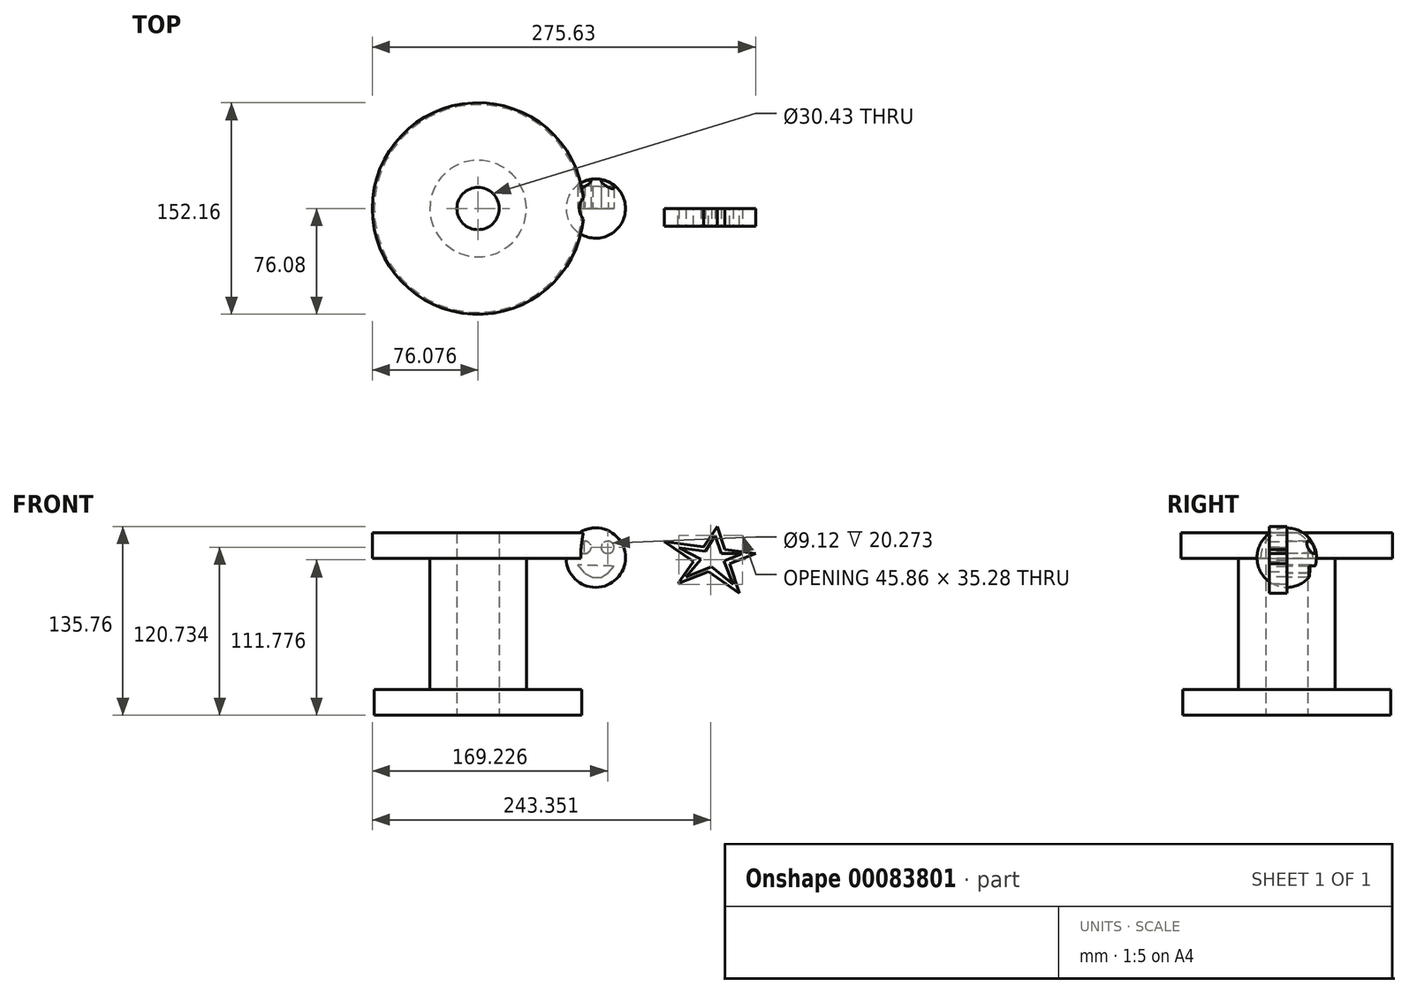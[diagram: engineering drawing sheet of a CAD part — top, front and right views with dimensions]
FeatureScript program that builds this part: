
annotation { "Feature Type Name" : "Feature", "Feature Type Description" : "" }
export const myFeature = defineFeature(function(context is Context, id is Id, definition is map)
    precondition{}
    {
        {
            var Q0;
            Q0=qCreatedBy(makeId("Front.planeOp"),FACE);
            var sketch = newSketch(context, id + "F0", { "sketchPlane" : qUnion([Q0])});
            skLineSegment(sketch, "E0", {"start": v(-32.02, -27.07) * mm, "end": v(-19.27, -67.24) * mm});
            skLineSegment(sketch, "E1", {"start": v(-19.27, -67.24) * mm, "end": v(-2.16, -25.66) * mm});
            skCircle(sketch, "E2", {"center": v(-17.49, -17.95) * mm, "radius": 17.16 * mm});
            skLineSegment(sketch, "E3", {"start": v(18.35, 23.13) * mm, "end": v(46.46, 64.2) * mm});
            skLineSegment(sketch, "E4", {"start": v(46.46, 64.2) * mm, "end": v(62.45, 16.23) * mm});
            skLineSegment(sketch, "E5", {"start": v(62.45, 16.23) * mm, "end": v(8.43, 53.21) * mm});
            skLineSegment(sketch, "E6", {"start": v(8.43, 53.21) * mm, "end": v(74.03, 44.9) * mm});
            skLineSegment(sketch, "E7", {"start": v(74.03, 44.9) * mm, "end": v(18.35, 23.13) * mm});
            skSolve(sketch);
        }
        {
            var Q0;
            Q0 = qSketchRegion(id + "F0", true);
            extrude(context, id + "F1", {"entities" : qUnion([Q0]), "depth" : 12.7 * mm});
        }
        {
            var Q0;
            Q0=makeQuery(id+"F1.opExtrude","CAP_FACE",FACE,{"disambiguationData":[OSD([sQuery(id+"F0.wireOp",EDGE,"E3"),sQuery(id+"F0.wireOp",EDGE,"E4"),sQuery(id+"F0.wireOp",EDGE,"E5"),sQuery(id+"F0.wireOp",EDGE,"E6"),sQuery(id+"F0.wireOp",EDGE,"E7")])],"isStart":false});
            var sketch = newSketch(context, id + "F2", { "sketchPlane" : qUnion([Q0])});
            skLineSegment(sketch, "E8", {"start": v(37.8, 46.38) * mm, "end": v(44.96, 57.86) * mm});
            skLineSegment(sketch, "E9", {"start": v(44.96, 57.86) * mm, "end": v(49.21, 44.66) * mm});
            skPoint(sketch, "E9.endSnap0", {"position": v(49.21, 55.95) * mm});
            skLineSegment(sketch, "E10", {"start": v(49.21, 44.66) * mm, "end": v(64.68, 44.66) * mm});
            skPoint(sketch, "E10.endSnap0", {"position": v(64.68, 41.25) * mm});
            skLineSegment(sketch, "E11", {"start": v(64.68, 44.66) * mm, "end": v(51.28, 39.42) * mm});
            skLineSegment(sketch, "E12", {"start": v(51.28, 39.42) * mm, "end": v(57.87, 22.58) * mm});
            skLineSegment(sketch, "E13", {"start": v(57.87, 22.58) * mm, "end": v(42.28, 35.26) * mm});
            skLineSegment(sketch, "E14", {"start": v(42.28, 35.26) * mm, "end": v(23.78, 28.03) * mm});
            skLineSegment(sketch, "E15", {"start": v(23.78, 28.03) * mm, "end": v(34.63, 40.65) * mm});
            skLineSegment(sketch, "E16", {"start": v(34.63, 40.65) * mm, "end": v(18.82, 48.96) * mm});
            skPoint(sketch, "E16.endSnap0", {"position": v(18.82, 46.1) * mm});
            skLineSegment(sketch, "E17", {"start": v(18.82, 48.96) * mm, "end": v(37.8, 46.38) * mm});
            skPoint(sketch, "E18", {"position": v(23.78, 31.06) * mm});
            skSolve(sketch);
        }
        {
            var Q0;
            Q0=makeQuery(id+"F2.imprint","IMPRINT",FACE,{"disambiguationData":[TD([[makeQuery(id+"F2.imprint","IMPRINT",EDGE,{"derivedFrom":sQuery(id+"F2.wireOp",EDGE,"E8")}),-1.0]])]});
            extrude(context, id + "F3", {"entities" : qUnion([Q0]), "operationType" : NewBodyOperationType.REMOVE, "endBound" : BoundingType.UP_TO_NEXT, "oppositeDirection" : true, "depth" : 25.4 * mm});
        }
        {
            var Q0;
            Q0=makeQuery(id+"F1.opExtrude","SWEPT_BODY",BODY,{"disambiguationData":[OSD([sQuery(id+"F0.wireOp",EDGE,"E0"),sQuery(id+"F0.wireOp",EDGE,"E1"),sQuery(id+"F0.wireOp",EDGE,"E2")])]});
            deleteBodies(context, id + "F4", {"entities" : qUnion([Q0])});
        }
        {
            var Q0;
            Q0=qCreatedBy(makeId("Front.planeOp"),FACE);
            var sketch = newSketch(context, id + "F5", { "sketchPlane" : qUnion([Q0])});
            skArc(sketch, "E19", {"start": v(-40.93, 63.15) * mm, "mid": v(-62.3, 41.79) * mm, "end": v(-40.93, 20.42) * mm});
            skLineSegment(sketch, "E20", {"start": v(-40.93, 41.79) * mm, "end": v(-40.93, 63.15) * mm});
            skLineSegment(sketch, "E21", {"start": v(-40.93, 41.79) * mm, "end": v(-40.93, 20.42) * mm});
            skSolve(sketch);
        }
        {
            var Q0;
            Q0 = qSketchRegion(id + "F5", true);
            var Q1;
            Q1=sQuery(id+"F5.wireOp",EDGE,"E21");
            revolve(context, id + "F6", {"entities" : qUnion([Q0]), "axis" : qUnion([Q1]), "revolveType" : RevolveType.FULL});
        }
        {
            var Q0;
            Q0=qCreatedBy(makeId("Front.planeOp"),FACE);
            var sketch = newSketch(context, id + "F7", { "sketchPlane" : qUnion([Q0])});
            skCircle(sketch, "E22", {"center": v(-48.8, 49.17) * mm, "radius": 4.5 * mm});
            skCircle(sketch, "E23", {"center": v(-32.37, 49.17) * mm, "radius": 4.56 * mm});
            skLineSegment(sketch, "E24", {"start": v(-53.96, 36.42) * mm, "end": v(-48.8, 30.53) * mm});
            skLineSegment(sketch, "E25", {"start": v(-48.8, 30.53) * mm, "end": v(-43.17, 27.6) * mm});
            skLineSegment(sketch, "E26", {"start": v(-43.17, 27.6) * mm, "end": v(-37.03, 27.6) * mm});
            skLineSegment(sketch, "E27", {"start": v(-37.03, 27.6) * mm, "end": v(-31.88, 30.78) * mm});
            skLineSegment(sketch, "E28", {"start": v(-31.88, 30.78) * mm, "end": v(-27.96, 35.69) * mm});
            skLineSegment(sketch, "E29", {"start": v(-27.96, 35.69) * mm, "end": v(-53.96, 36.42) * mm});
            skSolve(sketch);
        }
        {
            var Q0;
            Q0 = qSketchRegion(id + "F7", true);
            extrude(context, id + "F8", {"entities" : qUnion([Q0]), "operationType" : NewBodyOperationType.REMOVE, "endBound" : BoundingType.THROUGH_ALL, "oppositeDirection" : true, "depth" : 25.4 * mm});
        }
        {
            var Q0;
            Q0=qCreatedBy(makeId("Front.planeOp"),FACE);
            var sketch = newSketch(context, id + "F9", { "sketchPlane" : qUnion([Q0])});
            skLineSegment(sketch, "E30", {"start": v(-200.17, -53.01) * mm, "end": v(-160.23, -53.01) * mm});
            skLineSegment(sketch, "E31", {"start": v(-160.23, -53.01) * mm, "end": v(-160.23, 41.13) * mm});
            skLineSegment(sketch, "E32", {"start": v(-160.23, 41.13) * mm, "end": v(-201.6, 41.13) * mm});
            skLineSegment(sketch, "E33", {"start": v(-201.6, 41.13) * mm, "end": v(-201.6, 59.67) * mm});
            skLineSegment(sketch, "E34", {"start": v(-201.6, 59.67) * mm, "end": v(-140.74, 59.67) * mm});
            skLineSegment(sketch, "E35", {"start": v(-140.74, 59.67) * mm, "end": v(-140.74, -71.56) * mm});
            skLineSegment(sketch, "E36", {"start": v(-140.74, -71.56) * mm, "end": v(-200.17, -71.56) * mm});
            skLineSegment(sketch, "E37", {"start": v(-200.17, -71.56) * mm, "end": v(-200.17, -53.01) * mm});
            skLineSegment(sketch, "E38", {"start": v(-125.52, -89.15) * mm, "end": v(-125.52, 81.07) * mm});
            skSolve(sketch);
        }
        {
            var Q0;
            Q0=makeQuery(id+"F9.imprint","IMPRINT",FACE,{"disambiguationData":[TD([[makeQuery(id+"F9.imprint","IMPRINT",EDGE,{"derivedFrom":sQuery(id+"F9.wireOp",EDGE,"E30")}),-1.0]])]});
            var Q1;
            Q1=sQuery(id+"F9.wireOp",EDGE,"E38");
            revolve(context, id + "F10", {"operationType" : NewBodyOperationType.ADD, "entities" : qUnion([Q0]), "axis" : qUnion([Q1]), "revolveType" : RevolveType.FULL});
        }
    });
